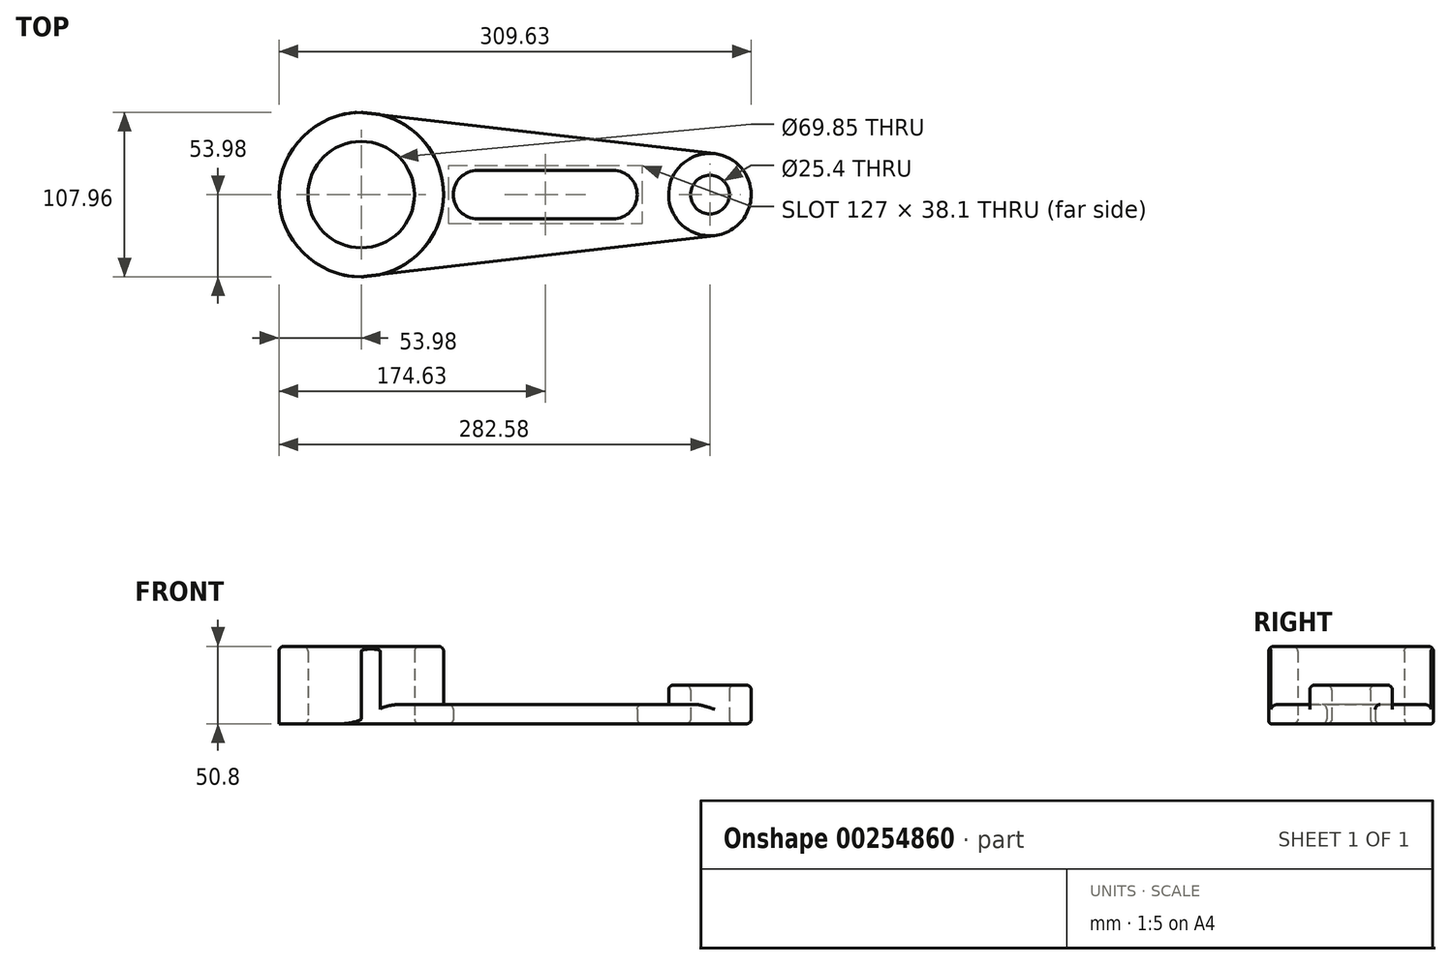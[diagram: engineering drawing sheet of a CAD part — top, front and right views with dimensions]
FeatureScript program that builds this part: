
annotation { "Feature Type Name" : "Feature", "Feature Type Description" : "" }
export const myFeature = defineFeature(function(context is Context, id is Id, definition is map)
    precondition{}
    {
        {
            var Q0;
            Q0=qCreatedBy(makeId("Top.planeOp"),FACE);
            var sketch = newSketch(context, id + "F0", { "sketchPlane" : qUnion([Q0])});
            skCircle(sketch, "E0", {"center": v(0, 0) * mm, "radius": 53.98 * mm});
            skCircle(sketch, "E1", {"center": v(0, 0) * mm, "radius": 34.93 * mm});
            skLineSegment(sketch, "E2", {"start": v(0, 0) * mm, "end": v(228.6, 0) * mm});
            skCircle(sketch, "E3", {"center": v(228.6, 0) * mm, "radius": 12.7 * mm});
            skCircle(sketch, "E4", {"center": v(228.6, 0) * mm, "radius": 27.05 * mm});
            skLineSegment(sketch, "E5", {"start": v(0, -53.97) * mm, "end": v(231.74, -26.87) * mm});
            skLineSegment(sketch, "E6.MirrorCS", {"start": v(0, 53.98) * mm, "end": v(231.74, 26.87) * mm});
            skLineSegment(sketch, "E7", {"start": v(0, -53.98) * mm, "end": v(76.2, -53.98) * mm, "construction": true});
            skLineSegment(sketch, "E8", {"start": v(76.2, -53.98) * mm, "end": v(76.2, 0) * mm, "construction": true});
            skLineSegment(sketch, "E9", {"start": v(76.2, -53.98) * mm, "end": v(165.1, -53.98) * mm, "construction": true});
            skLineSegment(sketch, "E10", {"start": v(165.1, -53.98) * mm, "end": v(165.1, 0) * mm, "construction": true});
            skCircle(sketch, "E11", {"center": v(165.1, 0) * mm, "radius": 15.88 * mm});
            skCircle(sketch, "E12", {"center": v(76.2, 0) * mm, "radius": 15.88 * mm});
            skLineSegment(sketch, "E13", {"start": v(76.2, 15.88) * mm, "end": v(165.1, 15.88) * mm});
            skLineSegment(sketch, "E14.MirrorCS", {"start": v(76.2, -15.88) * mm, "end": v(165.1, -15.88) * mm});
            skSolve(sketch);
        }
        {
            var Q0;
            Q0=makeQuery(id+"F0.imprint","IMPRINT",FACE,{"disambiguationData":[TD([[makeQuery(id+"F0.imprint","IMPRINT",EDGE,{"derivedFrom":sQuery(id+"F0.wireOp",EDGE,"E1")}),-1.0]])]});
            extrude(context, id + "F1", {"entities" : qUnion([Q0]), "depth" : 50.8 * mm});
        }
        {
            var Q0;
            {var subQ12=sQuery(id+"F0.wireOp",EDGE,"E14.MirrorCS");Q0=makeQuery(id+"F0.imprint","IMPRINT",FACE,{"disambiguationData":[TD([[makeQuery(id+"F0.imprint","IMPRINT",EDGE,{"derivedFrom":subQ12}),-1.0]])]});}
            var Q1;
            {var subQ11=sQuery(id+"F0.wireOp",EDGE,"E13");Q1=makeQuery(id+"F0.imprint","IMPRINT",FACE,{"disambiguationData":[TD([[makeQuery(id+"F0.imprint","IMPRINT",EDGE,{"derivedFrom":subQ11}),1.0]])]});}
            extrude(context, id + "F2", {"entities" : qUnion([Q0, Q1]), "operationType" : NewBodyOperationType.ADD, "depth" : 12.7 * mm});
        }
        {
            var Q0;
            Q0=makeQuery(id+"F0.imprint","IMPRINT",FACE,{"disambiguationData":[TD([[makeQuery(id+"F0.imprint","IMPRINT",EDGE,{"derivedFrom":sQuery(id+"F0.wireOp",EDGE,"E3")}),-1.0]])]});
            extrude(context, id + "F3", {"entities" : qUnion([Q0]), "operationType" : NewBodyOperationType.ADD, "depth" : 25.4 * mm});
        }
        {
            var Q0;
            {var subQ0=sQuery(id+"F0.wireOp",EDGE,"E0");var subQ1=makeQuery(id+"F0.imprint","INTERSECT",VERTEX,{"derivedFrom":[subQ0,sQuery(id+"F0.wireOp",EDGE,"E2")]});Q0=makeQuery(id+"F1.opExtrude","CAP_EDGE",EDGE,{"disambiguationData":[OSD([subQ0]),TDD([makeQuery(id+"F0.imprint","IMPRINT",EDGE,{"disambiguationData":[TD([[makeQuery(id+"F0.imprint","INTERSECT",VERTEX,{"disambiguationData":[OD(1.0)],"derivedFrom":[subQ0,sQuery(id+"F0.wireOp",EDGE,"E6.MirrorCS")]}),1.0]])],"derivedFrom":subQ0}),makeQuery(id+"F0.imprint","IMPRINT",EDGE,{"disambiguationData":[TD([[subQ1,1.0]])],"derivedFrom":subQ0})])],"isStart":false});}
            var Q1;
            Q1=makeQuery(id+"F3.opExtrude","CAP_EDGE",EDGE,{"disambiguationData":[OSD([sQuery(id+"F0.wireOp",EDGE,"E4")])],"isStart":false});
            var Q2;
            Q2=makeQuery(id+"F2.opExtrude","CAP_EDGE",EDGE,{"disambiguationData":[OSD([sQuery(id+"F0.wireOp",EDGE,"E6.MirrorCS")])],"isStart":false});
            var Q3;
            Q3=makeQuery(id+"F2.opExtrude","CAP_EDGE",EDGE,{"disambiguationData":[OSD([sQuery(id+"F0.wireOp",EDGE,"E5")])],"isStart":false});
            var Q4;
            Q4=makeQuery(id+"F2.opExtrude","SWEPT_FACE",FACE,{"disambiguationData":[OSD([sQuery(id+"F0.wireOp",EDGE,"E14.MirrorCS")])]});
            var Q5;
            {var subQ0=sQuery(id+"F0.wireOp",EDGE,"E6.MirrorCS");Q5=makeQuery(id+"F2.boolean.opBoolean","MERGE",EDGE,{"derivedFrom":[makeQuery(id+"F1.opExtrude","CAP_EDGE",EDGE,{"disambiguationData":[OSD([subQ0])],"isStart":true}),makeQuery(id+"F2.opExtrude","CAP_EDGE",EDGE,{"disambiguationData":[OSD([subQ0])],"isStart":true})]});}
            var Q6;
            {var subQ0=sQuery(id+"F0.wireOp",EDGE,"E5");Q6=makeQuery(id+"F2.boolean.opBoolean","MERGE",EDGE,{"derivedFrom":[makeQuery(id+"F1.opExtrude","CAP_EDGE",EDGE,{"disambiguationData":[OSD([subQ0])],"isStart":true}),makeQuery(id+"F2.opExtrude","CAP_EDGE",EDGE,{"disambiguationData":[OSD([subQ0])],"isStart":true})]});}
            var Q7;
            {var subQ0=sQuery(id+"F0.wireOp",EDGE,"E0");Q7=makeQuery(id+"F1.opExtrude","CAP_EDGE",EDGE,{"disambiguationData":[OSD([subQ0]),TDD([makeQuery(id+"F0.imprint","IMPRINT",EDGE,{"disambiguationData":[TD([[makeQuery(id+"F0.imprint","INTERSECT",VERTEX,{"disambiguationData":[OD(0.0)],"derivedFrom":[subQ0,sQuery(id+"F0.wireOp",EDGE,"E5")]}),1.0]])],"derivedFrom":subQ0})])],"isStart":true});}
            var Q8;
            Q8=makeQuery(id+"F1.opExtrude","CAP_EDGE",EDGE,{"disambiguationData":[OSD([sQuery(id+"F0.wireOp",EDGE,"E1")])],"isStart":true});
            var Q9;
            Q9=makeQuery(id+"F1.opExtrude","CAP_EDGE",EDGE,{"disambiguationData":[OSD([sQuery(id+"F0.wireOp",EDGE,"E1")])],"isStart":false});
            var Q10;
            Q10=makeQuery(id+"F3.opExtrude","CAP_EDGE",EDGE,{"disambiguationData":[OSD([sQuery(id+"F0.wireOp",EDGE,"E3")])],"isStart":false});
            var Q11;
            Q11=makeQuery(id+"F3.opExtrude","CAP_EDGE",EDGE,{"disambiguationData":[OSD([sQuery(id+"F0.wireOp",EDGE,"E3")])],"isStart":true});
            fillet(context, id + "F4", {"entities" : qUnion([Q0, Q1, Q2, Q3, Q4, Q5, Q6, Q7, Q8, Q9, Q10, Q11]), "radius" : 3.17 * mm, "tangentPropagation" : true, "allowEdgeOverflow" : false});
        }
    });
